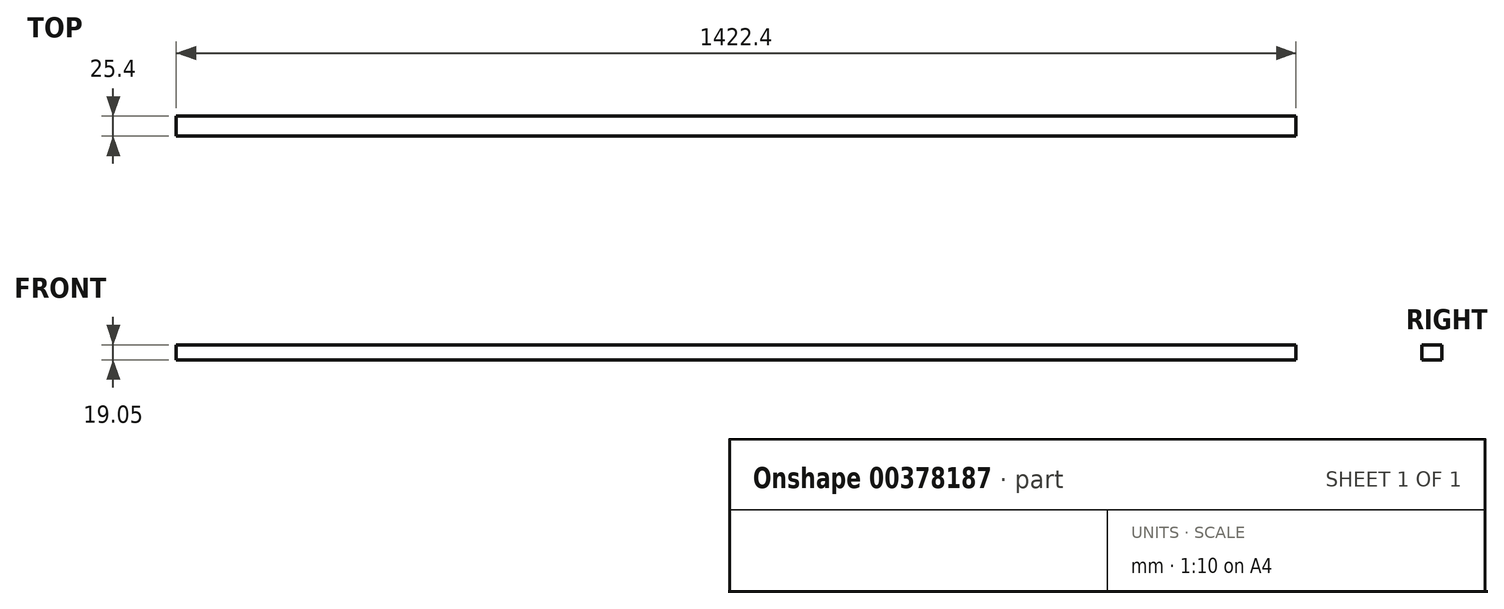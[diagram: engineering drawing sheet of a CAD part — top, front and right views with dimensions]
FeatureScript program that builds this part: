
annotation { "Feature Type Name" : "Feature", "Feature Type Description" : "" }
export const myFeature = defineFeature(function(context is Context, id is Id, definition is map)
    precondition{}
    {
        {
            var Q0;
            Q0=qCreatedBy(makeId("Top.planeOp"),FACE);
            var sketch = newSketch(context, id + "F0", { "sketchPlane" : qUnion([Q0])});
            skLineSegment(sketch, "E0.bottom", {"start": v(0, 0) * mm, "end": v(1422.4, 0) * mm});
            skLineSegment(sketch, "E0.top", {"start": v(0, -25.4) * mm, "end": v(1422.4, -25.4) * mm});
            skLineSegment(sketch, "E0.left", {"start": v(0, 0) * mm, "end": v(0, -25.4) * mm});
            skLineSegment(sketch, "E0.right", {"start": v(1422.4, 0) * mm, "end": v(1422.4, -25.4) * mm});
            skSolve(sketch);
        }
        {
            var Q0;
            Q0=makeQuery(id+"F0.imprint","IMPRINT",FACE,{"disambiguationData":[TD([[makeQuery(id+"F0.imprint","IMPRINT",EDGE,{"derivedFrom":sQuery(id+"F0.wireOp",EDGE,"E0.bottom")}),-1.0]])]});
            extrude(context, id + "F1", {"entities" : qUnion([Q0]), "depth" : 19.05 * mm});
        }
    });
